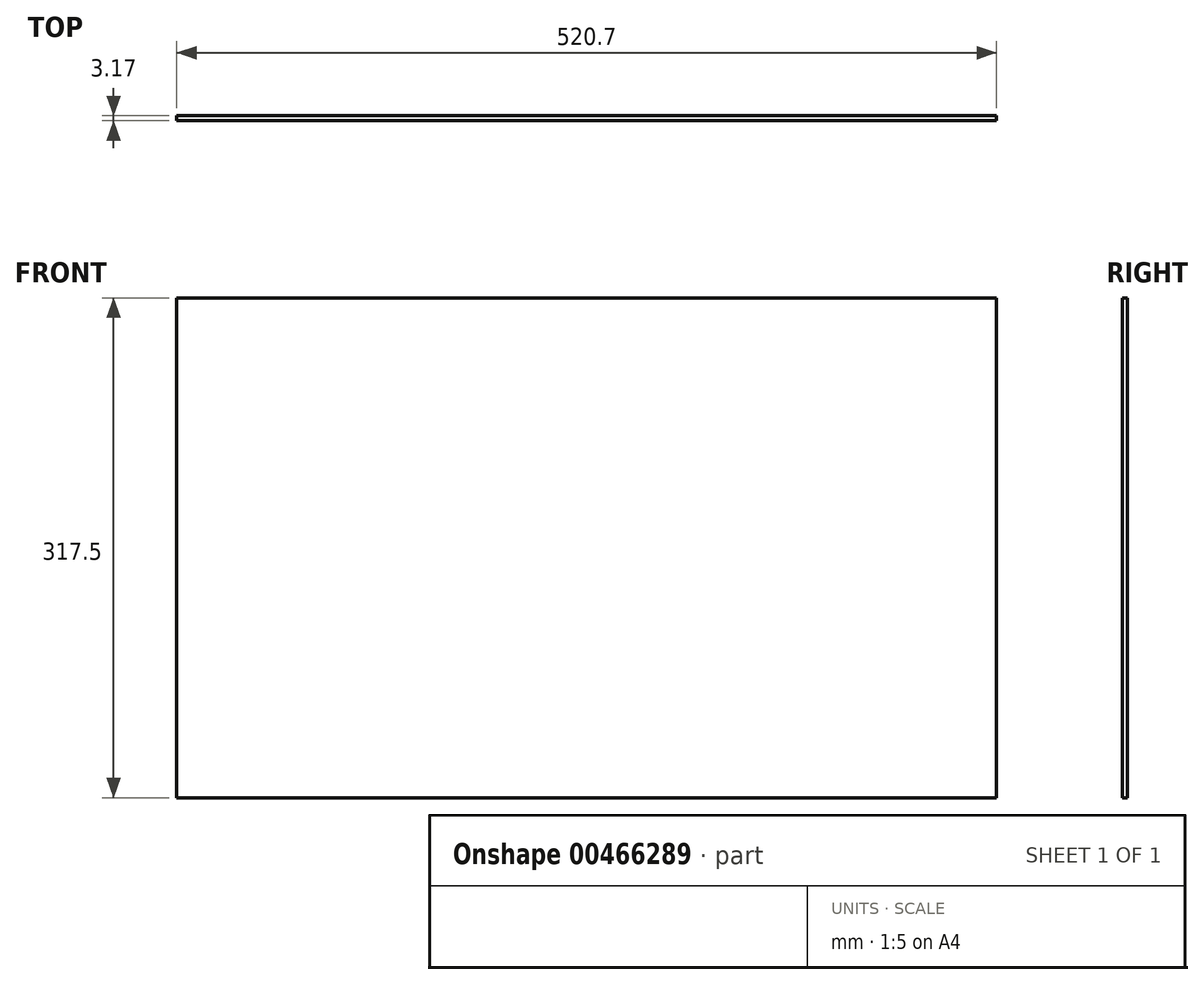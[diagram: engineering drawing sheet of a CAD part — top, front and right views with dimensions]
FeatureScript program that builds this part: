
annotation { "Feature Type Name" : "Feature", "Feature Type Description" : "" }
export const myFeature = defineFeature(function(context is Context, id is Id, definition is map)
    precondition{}
    {
        {
            var Q0;
            Q0=qCreatedBy(makeId("Front.planeOp"),FACE);
            var sketch = newSketch(context, id + "F0", { "sketchPlane" : qUnion([Q0])});
            skLineSegment(sketch, "E0", {"start": v(-367.72, 404.16) * mm, "end": v(152.98, 404.16) * mm});
            skLineSegment(sketch, "E1", {"start": v(152.98, 404.16) * mm, "end": v(152.98, 86.66) * mm});
            skLineSegment(sketch, "E2", {"start": v(152.98, 86.66) * mm, "end": v(-367.72, 86.66) * mm});
            skLineSegment(sketch, "E3", {"start": v(-367.72, 86.66) * mm, "end": v(-367.72, 404.16) * mm});
            skSolve(sketch);
        }
        {
            var Q0;
            Q0=qSketchRegion(id+"F0",true);
            extrude(context, id + "F1", {"entities" : qUnion([Q0]), "depth" : 3.17 * mm, "offsetDistance" : 25.4 * mm});
        }
    });
